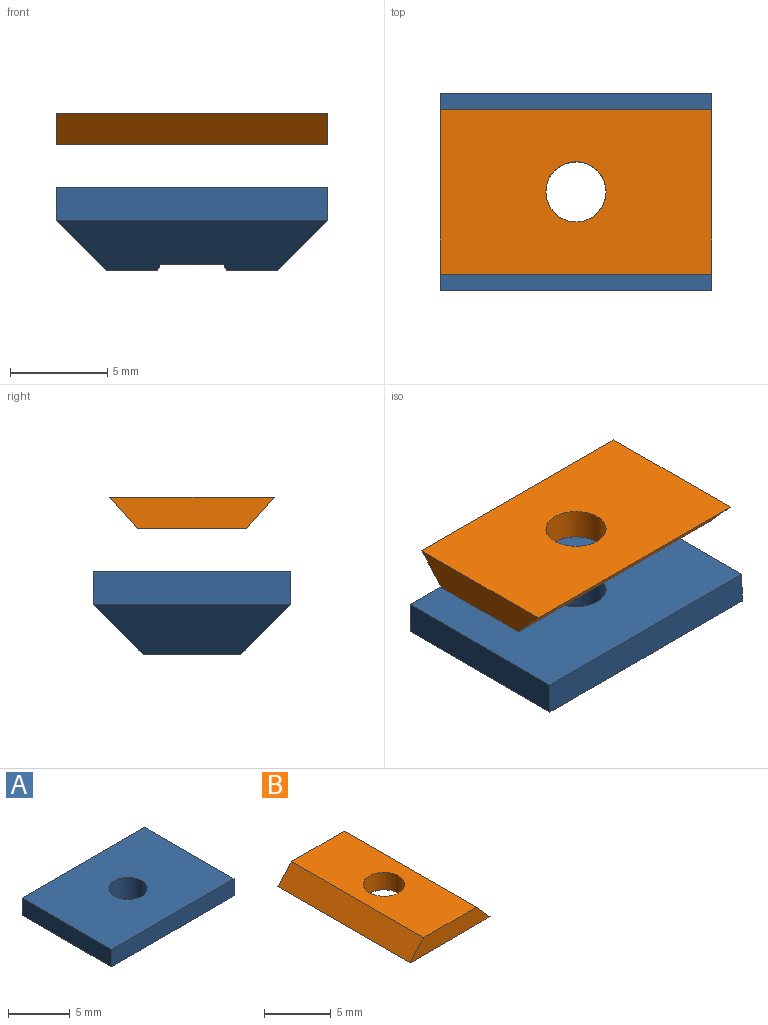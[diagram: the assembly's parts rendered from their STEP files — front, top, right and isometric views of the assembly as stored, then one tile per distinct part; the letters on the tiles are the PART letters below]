
ASSEMBLY  parts=2 mates=1
PART A: 19 faces, bbox 14x10.2x4.3 mm
  f0: plane 14x2.6mm, normal (0,-0.71,-0.71), area 40.5mm2, adj f2,f4,f5,f6,f7,f8,f9,f15
  f1: plane 14x2.6mm, normal (0,0.71,-0.71), area 40.5mm2, adj f2,f4,f5,f6,f10,f11,f12,f16
  f2: plane 5x2.61mm, normal (0,0,-1), area 9.4mm2, adj f0,f1,f5,f9,f10
  f3: cylinder r=1.55mm len=3.1mm, axis (0,0,-1), area 19.5mm2, adj f13,f18
  f4: plane 10.2x2.6mm, normal (0.71,0,-0.71), area 27.9mm2, adj f0,f1,f6,f14
  f5: plane 10.2x2.6mm, normal (-0.71,0,-0.71), area 27.9mm2, adj f0,f1,f2,f17
  f6: plane 5x2.61mm, normal (0,0,-1), area 9.4mm2, adj f0,f1,f4,f7,f12
  f7: plane 2.8x2.3mm, normal (-0.87,0.5,0), area 7.4mm2, adj f0,f6,f8,f12,f13
  f8: plane 3.23x2mm, normal (0,1,0), area 6.5mm2, adj f0,f7,f9,f13
  f9: plane 2.8x2.3mm, normal (0.87,0.5,0), area 7.4mm2, adj f0,f2,f8,f10,f13
  f10: plane 2.8x2.3mm, normal (0.87,-0.5,0), area 7.4mm2, adj f1,f2,f9,f11,f13
  f11: plane 3.23x2mm, normal (0,-1,0), area 6.5mm2, adj f1,f10,f12,f13
  f12: plane 2.8x2.3mm, normal (-0.87,-0.5,0), area 7.4mm2, adj f1,f6,f7,f11,f13
  f13: plane 6.47x5.6mm, normal (0,0,-1), area 19.6mm2, adj f3,f7,f8,f9,f10,f11,f12
  f14: plane 10.2x1.7mm, normal (1,0,0), area 17.3mm2, adj f4,f15,f16,f18
  f15: plane 14x1.7mm, normal (0,-1,0), area 23.8mm2, adj f0,f14,f17,f18
  f16: plane 14x1.7mm, normal (0,1,0), area 23.8mm2, adj f1,f14,f17,f18
  f17: plane 10.2x1.7mm, normal (-1,0,0), area 17.3mm2, adj f5,f15,f16,f18
  f18: plane 14x10.2mm, normal (0,0,1), area 135.3mm2, adj f3,f14,f15,f16,f17
PART B: 7 faces, bbox 8.5x14x1.6 mm
  f0: plane 14x1.6mm, normal (-0.74,0,0.67), area 30.1mm2, adj f1,f3,f4,f5
  f1: plane 14x8.48mm, normal (0,0,-1), area 111.2mm2, adj f0,f2,f4,f5,f6
  f2: plane 14x1.6mm, normal (0.74,0,0.67), area 30.1mm2, adj f1,f3,f4,f5
  f3: plane 14x5.6mm, normal (0,0,1), area 70.9mm2, adj f0,f2,f4,f5,f6
  f4: plane 8.48x1.6mm, normal (0,-1,0), area 11.3mm2, adj f0,f1,f2,f3
  f5: plane 8.48x1.6mm, normal (0,1,0), area 11.3mm2, adj f0,f1,f2,f3
  f6: cylinder r=1.55mm len=3.1mm, axis (0,0,1), area 15.6mm2, adj f1,f3
PLACE A t=(-29.93,-6.17,18.12)mm
PLACE B rot(axis=(-0.71,0.71,0),180deg) t=(-36.93,-5.9,23.63)mm
MATE slider A.f3 <-> B.f6  axis (0,0,-1) through (-29.93,-6.17,18.82)mm
